# Revit family: LeL Colorado 4.0
name_source: partatom
category: Lighting Fixtures
units: mm (PartAtom-declared; Revit-internal decimal feet)

## family parameters
Cut with Voids When Loaded = Yes
Host = Face
Light Source = No
Part Type = Normal
Room Calculation Point = No
Round Connector Dimension = Use Diameter
Shared = No

## types (5) — shared parameters
Accessories = WCCA10A0T
Alimentazione = 230 V
Apparent Load = 43 VA
CCT = 3000 K
CRI = 80
Default Elevation = 1219 mm
Description = Outdoor Linear Profile
Finish = LeL Black
IK = IK10
IP = IP65 IP67 IP69
Lamp = LED
Lenght = 625 mm  [stored 2.05052 ft]
Manufacturer = L&L Luce&Light
Model = CA40
Outercasing = 669 mm
Rated Power supply = 230 V
URL = https://www.lucelight.it
Wattage = 43 W
Weight = 5.60 kg

## per-type parameters (varying)
| type | Optic |
| 4.0 W 13°x65° 43W | COLORADO Light source : 4.0 W 13°x65° 43W |
| 4.0 L 37° 43W | COLORADO Light source : 4.0 L 37° 43W |
| 4.0 D 43W | COLORADO Light source : 4.0 D 43W |
| 4.0 M 25° 43W | COLORADO Light source : 4.0 M 25° 43W |
| 4.0 S 15° 43W | COLORADO Light source : 4.0 S 15° 43W |

note: [stored X ft] marks values corroborated as IEEE doubles in the binary element streams (Revit-internal decimal feet)

## geometry (parser evidence)
native form markers: Sweep x4
no freeform markers — native parametric forms only
